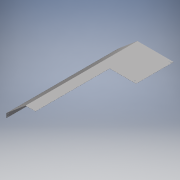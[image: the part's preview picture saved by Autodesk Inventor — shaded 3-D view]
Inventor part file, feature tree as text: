
AUTODESK INVENTOR PART (.ipt)
format: ipt  version: 2016 (Build 200138000, 138)  size: 213,504 bytes
history: native  units: mm
features: sheet_metal_op x7, sketch x5, other x4, hole x2
ambient origin geometry x8: Origin, YZ Plane, XZ Plane, XY Plane, X Axis, Y Axis, Z Axis, Center Point
bodies: Solid1 (feature_tree)
feature tree (18):
  sheet_metal_op  "Face1"
  sheet_metal_op  "Flange1"
  sheet_metal_op  "Flange2"
  hole  "Hole2"  [1 undecoded]
  hole  "Hole3"  [1 undecoded]
  sketch  "Sketch1"  dims[d0=150.0mm d1=1695.0mm]
  other  "Plate1"
  sketch  "Sketch2"  dims[d2=550.0mm d3=570.0mm]
  other  "Plate2"
  sheet_metal_op  "Bend1"
  sheet_metal_op  "Corner1"
  sketch  "Sketch4"  dims[d4=1.6mm]
  other  "Plate3"
  sheet_metal_op  "Bend2"
  sheet_metal_op  "Corner2"
  sketch  "Sketch6"  dims[d5=1.6mm]
  sketch  "Sketch7"  dims[d6=0.8mm d7=3.2mm d8=1.6mm d9=380.0mm d10=6.981317mm d11=1.6mm d12=6.4mm d13=1.6mm d14=1.6mm d28=1.6mm d29=0.8mm d30=3.2mm d31=1.6mm d32=65.0mm d33=-8.726646mm d34=1.6mm d35=6.4mm d36=1.6mm d37=1.6mm d39=60.0mm d40=12.0mm d41=12.0mm d42=25.0mm d43=25.0mm d44=15.0mm d45=15.0mm d46=12.0mm d47=12.0mm d48=25.0mm d49=25.0mm d50=12.0mm d51=6.0mm d52=4.0mm d53=2.0mm d54=90.0deg d55=1.6mm d56=20.594885mm d57=60.0mm d58=12.0mm d59=12.0mm d60=15.0mm d61=15.0mm d62=25.0mm d63=25.0mm d64=12.0mm d65=12.0mm d66=25.0mm d67=25.0mm d68=12.0mm d69=6.0mm d70=4.0mm d71=2.0mm d72=90.0deg d73=1.6mm d74=20.594885mm d75=15.0mm d76=15.0mm d77=15.0mm d78=15.0mm]
  other  "Definition1"
note: 2 required parameter values undecoded (feature->parameter linkage not recoverable at this tier; creation-order binding heuristic only, values carry confidence <= 0.55)
